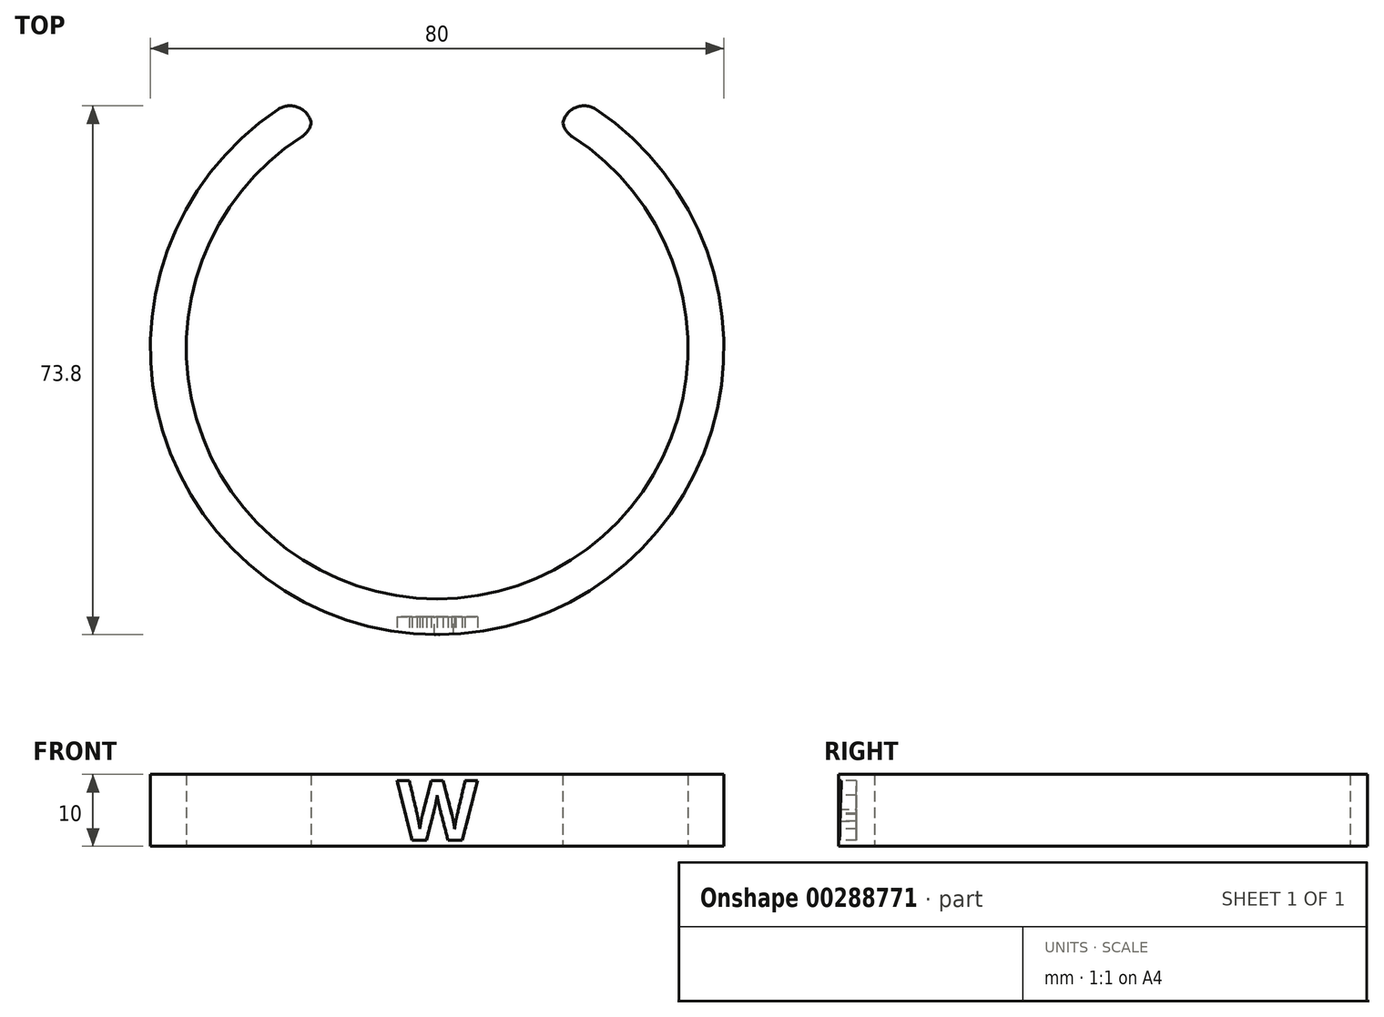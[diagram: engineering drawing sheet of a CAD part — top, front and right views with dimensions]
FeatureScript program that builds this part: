
annotation { "Feature Type Name" : "Feature", "Feature Type Description" : "" }
export const myFeature = defineFeature(function(context is Context, id is Id, definition is map)
    precondition{}
    {
        {
            var Q0;
            Q0=qCreatedBy(makeId("Top.planeOp"),FACE);
            var sketch = newSketch(context, id + "F0", { "sketchPlane" : qUnion([Q0])});
            skCircle(sketch, "E0", {"center": v(0, 0) * mm, "radius": 35 * mm});
            skCircle(sketch, "E1", {"center": v(0, 0) * mm, "radius": 40 * mm});
            skLineSegment(sketch, "E2", {"start": v(0, 0) * mm, "end": v(0, 35) * mm, "construction": true});
            skLineSegment(sketch, "E3", {"start": v(-17.5, 30.31) * mm, "end": v(17.5, 30.31) * mm, "construction": true});
            skLineSegment(sketch, "E4", {"start": v(-17.5, 30.31) * mm, "end": v(-17.5, 35.97) * mm});
            skLineSegment(sketch, "E5.MirrorCS", {"start": v(17.5, 30.31) * mm, "end": v(17.5, 35.97) * mm});
            skLineSegment(sketch, "E6", {"start": v(0, 0) * mm, "end": v(0, -42) * mm, "construction": true});
            skLineSegment(sketch, "E7.bottom", {"start": v(7.5, -42.5) * mm, "end": v(-7.5, -42.5) * mm});
            skLineSegment(sketch, "E7.top", {"start": v(7.5, -41.5) * mm, "end": v(-7.5, -41.5) * mm});
            skLineSegment(sketch, "E7.left", {"start": v(7.5, -42.5) * mm, "end": v(7.5, -41.5) * mm});
            skLineSegment(sketch, "E7.right", {"start": v(-7.5, -42.5) * mm, "end": v(-7.5, -41.5) * mm});
            skPoint(sketch, "E7.middle", {"position": v(0, -42) * mm});
            skSolve(sketch);
        }
        {
            var Q0;
            {var subQ0=sQuery(id+"F0.wireOp",EDGE,"E4");Q0=makeQuery(id+"F0.imprint","IMPRINT",FACE,{"disambiguationData":[TD([[makeQuery(id+"F0.imprint","IMPRINT",EDGE,{"derivedFrom":subQ0}),1.0]])]});}
            extrude(context, id + "F1", {"entities" : qUnion([Q0]), "depth" : 10 * mm});
        }
        {
            var Q0;
            Q0=makeQuery(id+"F0.imprint","IMPRINT",FACE,{"disambiguationData":[TD([[makeQuery(id+"F0.imprint","IMPRINT",EDGE,{"derivedFrom":sQuery(id+"F0.wireOp",EDGE,"E7.bottom")}),-1.0]])]});
            extrude(context, id + "F2", {"entities" : qUnion([Q0]), "depth" : 10 * mm});
        }
        {
            var Q0;
            Q0=makeQuery(id+"F2.opExtrude","SWEPT_FACE",FACE,{"disambiguationData":[OSD([sQuery(id+"F0.wireOp",EDGE,"E7.bottom")])]});
            var sketch = newSketch(context, id + "F3", { "sketchPlane" : qUnion([Q0])});
            skText(sketch, "E8", { "text": "W", "fontName": "OpenSans-Bold.ttf"});
            skLineSegment(sketch, "E9", {"start": v(0, 10) * mm, "end": v(0, 0) * mm, "construction": true});
            skLineSegment(sketch, "E10", {"start": v(0, 10) * mm, "end": v(0, 9.19) * mm, "construction": true});
            skLineSegment(sketch, "E11", {"start": v(0, 0.81) * mm, "end": v(0, 0) * mm, "construction": true});
            skLineSegment(sketch, "E12", {"start": v(6.4, 5) * mm, "end": v(7.5, 5) * mm, "construction": true});
            const initialGuessF3  = {"E8": [-0.0056, 0.00081, 1, 0, 0.00837]};
            skSetInitialGuess(sketch, initialGuessF3);
            skSolve(sketch);
        }
        {
            var Q0;
            Q0=makeQuery(id+"F3.imprint","IMPRINT",FACE,{"disambiguationData":[TD([[makeQuery(id+"F3.imprint","IMPRINT",EDGE,{"derivedFrom":sQuery(id+"F3.wireOp",EDGE,"E8.sketch_text.stroke-0")}),-1.0]])]});
            extrude(context, id + "F4", {"entities" : qUnion([Q0]), "operationType" : NewBodyOperationType.REMOVE, "oppositeDirection" : true, "depth" : 5 * mm});
        }
        {
            var Q0;
            Q0=makeQuery(id+"F2.opExtrude","SWEPT_BODY",BODY,{"disambiguationData":[OSD([sQuery(id+"F0.wireOp",EDGE,"E7.bottom"),sQuery(id+"F0.wireOp",EDGE,"E7.top"),sQuery(id+"F0.wireOp",EDGE,"E7.left"),sQuery(id+"F0.wireOp",EDGE,"E7.right")])]});
            deleteBodies(context, id + "F5", {"entities" : qUnion([Q0])});
        }
        {
            var Q0;
            Q0=makeQuery(id+"F1.opExtrude","SWEPT_EDGE",EDGE,{"disambiguationData":[OSD([sQuery(id+"F0.wireOp",EDGE,"E0"),sQuery(id+"F0.wireOp",EDGE,"E5.MirrorCS")])]});
            var Q1;
            Q1=makeQuery(id+"F1.opExtrude","SWEPT_EDGE",EDGE,{"disambiguationData":[OSD([sQuery(id+"F0.wireOp",EDGE,"E1"),sQuery(id+"F0.wireOp",EDGE,"E5.MirrorCS")])]});
            var Q2;
            Q2=makeQuery(id+"F1.opExtrude","SWEPT_EDGE",EDGE,{"disambiguationData":[OSD([sQuery(id+"F0.wireOp",EDGE,"E0"),sQuery(id+"F0.wireOp",EDGE,"E4")])]});
            var Q3;
            Q3=makeQuery(id+"F1.opExtrude","SWEPT_EDGE",EDGE,{"disambiguationData":[OSD([sQuery(id+"F0.wireOp",EDGE,"E1"),sQuery(id+"F0.wireOp",EDGE,"E4")])]});
            fillet(context, id + "F6", {"entities" : qUnion([Q0, Q1, Q2, Q3]), "radius" : 3 * mm, "tangentPropagation" : true, "allowEdgeOverflow" : false});
        }
    });
